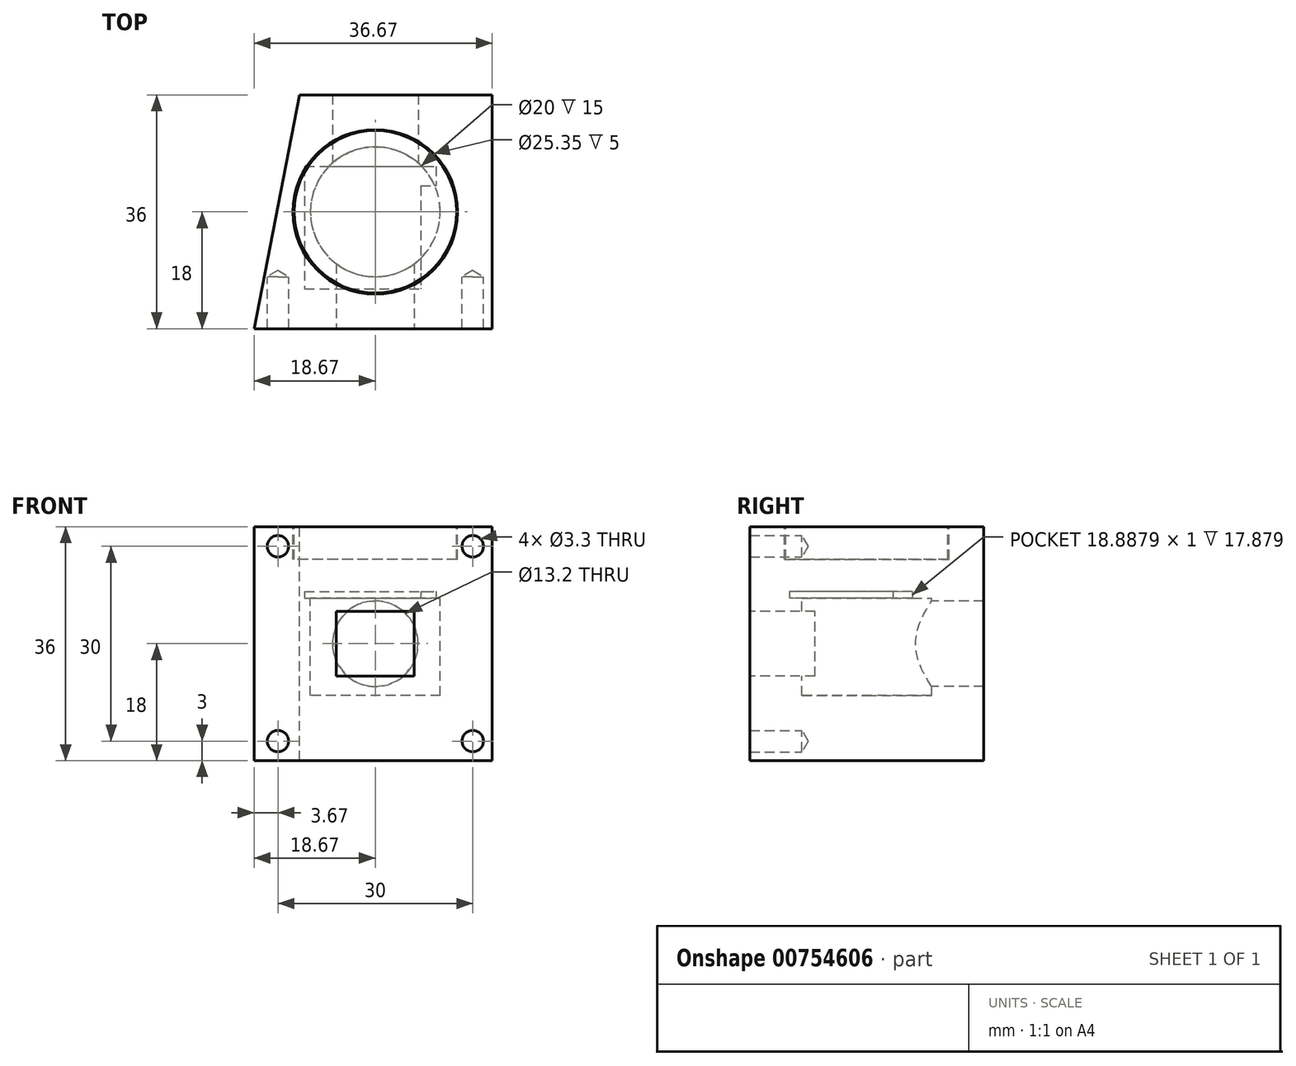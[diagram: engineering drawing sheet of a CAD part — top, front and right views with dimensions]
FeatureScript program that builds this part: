
annotation { "Feature Type Name" : "Feature", "Feature Type Description" : "" }
export const myFeature = defineFeature(function(context is Context, id is Id, definition is map)
    precondition{}
    {
        {
            var Q0;
            Q0=qCreatedBy(makeId("Top.planeOp"),FACE);
            var sketch = newSketch(context, id + "F0", { "sketchPlane" : qUnion([Q0])});
            skLineSegment(sketch, "E0", {"start": v(0, 0) * mm, "end": v(0, 120) * mm});
            skLineSegment(sketch, "E1", {"start": v(0, 120) * mm, "end": v(-32.87, -49.1) * mm});
            skSolve(sketch);
        }
        {
            var Q0;
            Q0=qCreatedBy(makeId("Front.planeOp"),FACE);
            var sketch = newSketch(context, id + "F1", { "sketchPlane" : qUnion([Q0])});
            skLineSegment(sketch, "E2.bottom", {"start": v(-18, 18) * mm, "end": v(18, 18) * mm});
            skLineSegment(sketch, "E2.top", {"start": v(-18, -18) * mm, "end": v(18, -18) * mm});
            skLineSegment(sketch, "E2.left", {"start": v(-18, 18) * mm, "end": v(-18, -18) * mm});
            skLineSegment(sketch, "E2.right", {"start": v(18, 18) * mm, "end": v(18, -18) * mm});
            skLineSegment(sketch, "E3", {"start": v(-18, 18) * mm, "end": v(18, -18) * mm});
            skSolve(sketch);
        }
        {
            var Q0;
            Q0 = qSketchRegion(id + "F1", true);
            extrude(context, id + "F2", {"entities" : qUnion([Q0]), "depth" : 36 * mm, "offsetDistance" : 25.4 * mm, "symmetric" : true});
        }
        {
            var Q0;
            Q0=makeQuery(id+"F2.opExtrude","CAP_FACE",FACE,{"disambiguationData":[OSD([sQuery(id+"F1.wireOp",EDGE,"E2.bottom"),sQuery(id+"F1.wireOp",EDGE,"E2.top"),sQuery(id+"F1.wireOp",EDGE,"E2.left"),sQuery(id+"F1.wireOp",EDGE,"E2.right")])],"isStart":false});
            var sketch = newSketch(context, id + "F3", { "sketchPlane" : qUnion([Q0])});
            skLineSegment(sketch, "E4.bottom", {"start": v(15, 15) * mm, "end": v(-15, 15) * mm});
            skLineSegment(sketch, "E4.top", {"start": v(15, -15) * mm, "end": v(-15, -15) * mm});
            skLineSegment(sketch, "E4.left", {"start": v(15, 15) * mm, "end": v(15, -15) * mm});
            skLineSegment(sketch, "E4.right", {"start": v(-15, 15) * mm, "end": v(-15, -15) * mm});
            skLineSegment(sketch, "E5", {"start": v(-15, 15) * mm, "end": v(15, -15) * mm});
            skSolve(sketch);
        }
        {
            var Q0;
            Q0=sQuery(id+"F3.wireOp",VERTEX,"E4.right.start");
            var Q1;
            Q1=sQuery(id+"F3.wireOp",VERTEX,"E4.left.start");
            var Q2;
            Q2=sQuery(id+"F3.wireOp",VERTEX,"E4.left.end");
            var Q3;
            Q3=sQuery(id+"F3.wireOp",VERTEX,"E4.top.end");
            var Q4;
            Q4=makeQuery(id+"F2.opExtrude","SWEPT_BODY",BODY,{"disambiguationData":[OSD([sQuery(id+"F1.wireOp",EDGE,"E2.bottom"),sQuery(id+"F1.wireOp",EDGE,"E2.top"),sQuery(id+"F1.wireOp",EDGE,"E2.left"),sQuery(id+"F1.wireOp",EDGE,"E2.right")])]});
            hole(context, id + "F4", {"style" : HoleStyle.SIMPLE, "endStyle" : HoleEndStyle.BLIND, "standardTappedOrClearance" : lookupTablePath({ "standard" : "ISO", "fit" : "Normal", "size" : "M3", "type" : "Clearance" }), "standardBlindInLast" : lookupTablePath({ "fit" : "Standard", "standard" : "ISO", "size" : "M3", "type" : "Clearance" }), "holeDiameter" : 3.3 * mm, "majorDiameter" : 5 * mm, "holeDepth" : 8 * mm, "isTappedThrough" : true, "tappedDepth" : 12 * mm, "tapClearance" : 3, "locations" : qUnion([Q0, Q1, Q2, Q3]), "scope" : qUnion([Q4]), "startStyle" : HoleStartStyle.SKETCH});
        }
        {
            var Q0;
            Q0=makeQuery(id+"F2.opExtrude","CAP_FACE",FACE,{"disambiguationData":[OSD([sQuery(id+"F1.wireOp",EDGE,"E2.bottom"),sQuery(id+"F1.wireOp",EDGE,"E2.top"),sQuery(id+"F1.wireOp",EDGE,"E2.left"),sQuery(id+"F1.wireOp",EDGE,"E2.right")])],"isStart":false});
            var sketch = newSketch(context, id + "F5", { "sketchPlane" : qUnion([Q0])});
            skLineSegment(sketch, "E6.bottom", {"start": v(6, -5) * mm, "end": v(-6, -5) * mm});
            skLineSegment(sketch, "E6.top", {"start": v(6, 5) * mm, "end": v(-6, 5) * mm});
            skLineSegment(sketch, "E6.left", {"start": v(6, -5) * mm, "end": v(6, 5) * mm});
            skLineSegment(sketch, "E6.right", {"start": v(-6, -5) * mm, "end": v(-6, 5) * mm});
            skPoint(sketch, "E6.middle", {"position": v(0, 0) * mm});
            skSolve(sketch);
        }
        {
            var Q0;
            Q0 = qSketchRegion(id + "F5", true);
            extrude(context, id + "F6", {"entities" : qUnion([Q0]), "operationType" : NewBodyOperationType.REMOVE, "oppositeDirection" : true, "depth" : 15 * mm, "offsetDistance" : 25 * mm});
        }
        {
            var Q0;
            Q0=qCreatedBy(makeId("Right.planeOp"),FACE);
            var sketch = newSketch(context, id + "F7", { "sketchPlane" : qUnion([Q0])});
            skLineSegment(sketch, "E7", {"start": v(0, 0) * mm, "end": v(0, 34.43) * mm});
            skSolve(sketch);
        }
        {
            var Q0;
            Q0=makeQuery(id+"F2.opExtrude","SWEPT_FACE",FACE,{"disambiguationData":[OSD([sQuery(id+"F1.wireOp",EDGE,"E2.bottom")])]});
            var sketch = newSketch(context, id + "F8", { "sketchPlane" : qUnion([Q0])});
            skCircle(sketch, "E8", {"center": v(0, 0) * mm, "radius": 10 * mm});
            skSolve(sketch);
        }
        {
            var Q0;
            Q0 = qSketchRegion(id + "F8", true);
            extrude(context, id + "F9", {"entities" : qUnion([Q0]), "operationType" : NewBodyOperationType.REMOVE, "oppositeDirection" : true, "depth" : (18 + 7 + 1) * mm, "offsetDistance" : 25 * mm});
        }
        {
            var Q0;
            Q0=makeQuery(id+"F2.opExtrude","CAP_FACE",FACE,{"disambiguationData":[OSD([sQuery(id+"F1.wireOp",EDGE,"E2.bottom"),sQuery(id+"F1.wireOp",EDGE,"E2.top"),sQuery(id+"F1.wireOp",EDGE,"E2.left"),sQuery(id+"F1.wireOp",EDGE,"E2.right")])],"isStart":true});
            var sketch = newSketch(context, id + "F10", { "sketchPlane" : qUnion([Q0])});
            skPoint(sketch, "E9", {"position": v(0, 0) * mm});
            skSolve(sketch);
        }
        {
            var Q0;
            Q0=sQuery(id+"F10.wireOp",VERTEX,"E9");
            var Q1;
            Q1=makeQuery(id+"F2.opExtrude","SWEPT_BODY",BODY,{"disambiguationData":[OSD([sQuery(id+"F1.wireOp",EDGE,"E2.bottom"),sQuery(id+"F1.wireOp",EDGE,"E2.top"),sQuery(id+"F1.wireOp",EDGE,"E2.left"),sQuery(id+"F1.wireOp",EDGE,"E2.right")])]});
            hole(context, id + "F11", {"style" : HoleStyle.SIMPLE, "endStyle" : HoleEndStyle.BLIND, "standardTappedOrClearance" : lookupTablePath({ "standard" : "ISO", "fit" : "Normal", "size" : "M12", "type" : "Clearance" }), "standardBlindInLast" : lookupTablePath({ "fit" : "Standard", "standard" : "ISO", "size" : "M12", "type" : "Clearance" }), "holeDiameter" : 13.2 * mm, "majorDiameter" : 5 * mm, "holeDepth" : 20 * mm, "isTappedThrough" : true, "tappedDepth" : 12 * mm, "tapClearance" : 3, "locations" : qUnion([Q0]), "scope" : qUnion([Q1]), "startStyle" : HoleStartStyle.SKETCH});
        }
        {
            var Q0;
            Q0=makeQuery(id+"F2.opExtrude","SWEPT_FACE",FACE,{"disambiguationData":[OSD([sQuery(id+"F1.wireOp",EDGE,"E2.bottom")])]});
            var sketch = newSketch(context, id + "F12", { "sketchPlane" : qUnion([Q0])});
            skCircle(sketch, "E10", {"center": v(0, 0) * mm, "radius": 12.68 * mm});
            skSolve(sketch);
        }
        {
            var Q0;
            Q0 = qSketchRegion(id + "F12", true);
            extrude(context, id + "F13", {"entities" : qUnion([Q0]), "operationType" : NewBodyOperationType.REMOVE, "oppositeDirection" : true, "depth" : 5 * mm, "offsetDistance" : 25 * mm});
        }
        {
            var Q0;
            Q0=makeQuery(id+"F2.opExtrude","SWEPT_FACE",FACE,{"disambiguationData":[OSD([sQuery(id+"F1.wireOp",EDGE,"E2.left")])]});
            extrude(context, id + "F14", {"entities" : qUnion([Q0]), "operationType" : NewBodyOperationType.ADD, "depth" : 16 * mm, "offsetDistance" : 25 * mm});
        }
        {
            var Q0;
            {var subQ0=sQuery(id+"F1.wireOp",EDGE,"E2.bottom");Q0=makeQuery(id+"F14.boolean.opBoolean","MERGE",FACE,{"derivedFrom":[makeQuery(id+"F2.opExtrude","SWEPT_FACE",FACE,{"disambiguationData":[OSD([subQ0])]}),makeQuery(id+"F14.opExtrude","SWEPT_FACE",FACE,{"disambiguationData":[OSD([subQ0,sQuery(id+"F1.wireOp",EDGE,"E2.left"),sQuery(id+"F1.wireOp",EDGE,"E3")])]})]});}
            var sketch = newSketch(context, id + "F15", { "sketchPlane" : qUnion([Q0])});
            skLineSegment(sketch, "E11", {"start": v(-11.68, 18) * mm, "end": v(-18.67, -18) * mm});
            skLineSegment(sketch, "E12", {"start": v(-18.67, -18) * mm, "end": v(-34, -18) * mm});
            skLineSegment(sketch, "E13", {"start": v(-34, -18) * mm, "end": v(-34, 18) * mm});
            skLineSegment(sketch, "E14", {"start": v(-34, 18) * mm, "end": v(-11.68, 18) * mm});
            skSolve(sketch);
        }
        {
            var Q0;
            Q0 = qSketchRegion(id + "F15", true);
            extrude(context, id + "F16", {"entities" : qUnion([Q0]), "operationType" : NewBodyOperationType.REMOVE, "endBound" : BoundingType.THROUGH_ALL, "oppositeDirection" : true, "depth" : 25 * mm, "offsetDistance" : 25 * mm});
        }
        {
            var Q0;
            {var subQ0=sQuery(id+"F1.wireOp",EDGE,"E2.bottom");Q0=makeQuery(id+"F14.boolean.opBoolean","MERGE",FACE,{"derivedFrom":[makeQuery(id+"F2.opExtrude","SWEPT_FACE",FACE,{"disambiguationData":[OSD([subQ0])]}),makeQuery(id+"F14.opExtrude","SWEPT_FACE",FACE,{"disambiguationData":[OSD([subQ0,sQuery(id+"F1.wireOp",EDGE,"E2.left"),sQuery(id+"F1.wireOp",EDGE,"E3")])]})]});}
            var sketch = newSketch(context, id + "F17", { "sketchPlane" : qUnion([Q0])});
            skCircle(sketch, "E15", {"center": v(0, 0) * mm, "radius": 12.5 * mm});
            skSolve(sketch);
        }
        {
            var Q0;
            Q0 = qSketchRegion(id + "F17", true);
            extrude(context, id + "F18", {"entities" : qUnion([Q0]), "oppositeDirection" : true, "depth" : 5 * mm, "offsetDistance" : 25 * mm});
        }
        {
            var Q0;
            Q0=makeQuery(id+"F18.opExtrude","CAP_FACE",FACE,{"disambiguationData":[OSD([sQuery(id+"F17.wireOp",EDGE,"E15")])],"isStart":false});
            var sketch = newSketch(context, id + "F19", { "sketchPlane" : qUnion([Q0])});
            skCircle(sketch, "E16", {"center": v(0, 0) * mm, "radius": 10 * mm});
            skSolve(sketch);
        }
        {
            var Q0;
            Q0 = qSketchRegion(id + "F19", true);
            extrude(context, id + "F20", {"entities" : qUnion([Q0]), "operationType" : NewBodyOperationType.ADD, "depth" : (38 / 2 - 5 - 8) * mm, "offsetDistance" : 25 * mm});
        }
        {
            var Q0;
            Q0=makeQuery(id+"F20.opExtrude","CAP_FACE",FACE,{"disambiguationData":[OSD([sQuery(id+"F19.wireOp",EDGE,"E16")])],"isStart":false});
            var sketch = newSketch(context, id + "F21", { "sketchPlane" : qUnion([Q0])});
            skLineSegment(sketch, "E17.bottom", {"start": v(-10.88, -7) * mm, "end": v(7, -7) * mm});
            skLineSegment(sketch, "E17.top", {"start": v(-10.88, 11.89) * mm, "end": v(7, 11.89) * mm});
            skLineSegment(sketch, "E17.left", {"start": v(-10.88, -7) * mm, "end": v(-10.88, 11.89) * mm});
            skLineSegment(sketch, "E17.right", {"start": v(7, -4) * mm, "end": v(7, 11.89) * mm});
            skLineSegment(sketch, "E18.bottom", {"start": v(7, -7) * mm, "end": v(9.35, -7) * mm});
            skLineSegment(sketch, "E18.top", {"start": v(7, -4) * mm, "end": v(9.35, -4) * mm});
            skLineSegment(sketch, "E18.right", {"start": v(9.35, -7) * mm, "end": v(9.35, -4) * mm});
            skSolve(sketch);
        }
        {
            var Q0;
            Q0 = qSketchRegion(id + "F21", true);
            extrude(context, id + "F22", {"entities" : qUnion([Q0]), "operationType" : NewBodyOperationType.REMOVE, "oppositeDirection" : true, "depth" : 1 * mm, "offsetDistance" : 25 * mm});
        }
        {
            var Q0;
            Q0=sQuery(id+"F0.wireOp",VERTEX,"E1.end");
            var Q1;
            Q1=sQuery(id+"F0.wireOp",EDGE,"E1");
            cPlane(context, id + "F23", {"entities" : qUnion([Q0, Q1]), "cplaneType" : CPlaneType.LINE_POINT, "offset" : 25 * mm, "width" : 150 * mm, "height" : 150 * mm});
        }
    });
